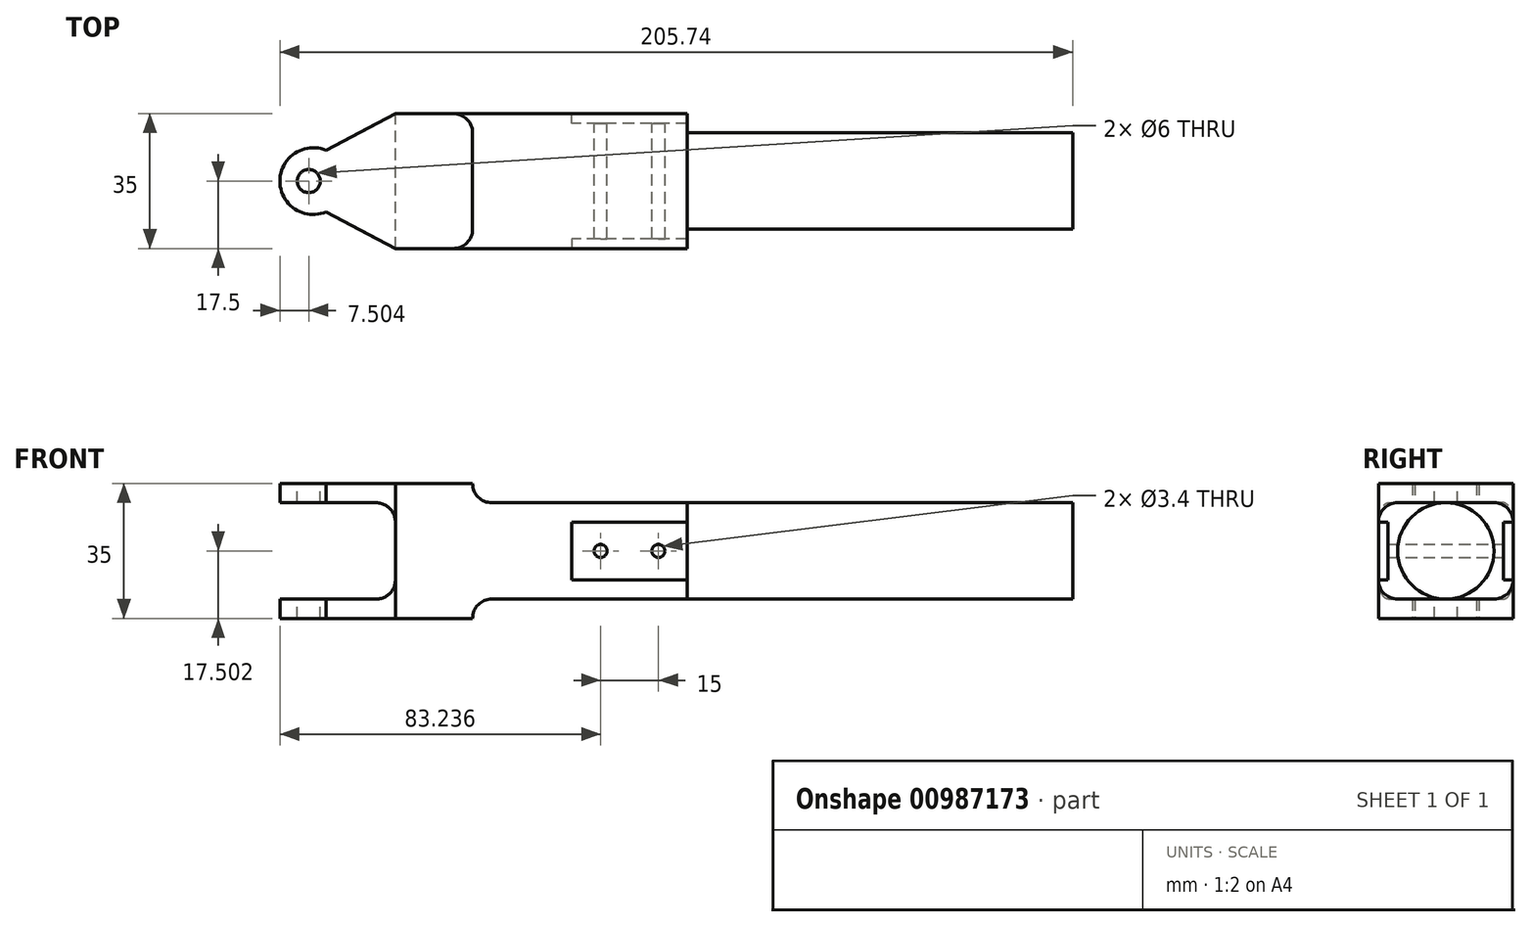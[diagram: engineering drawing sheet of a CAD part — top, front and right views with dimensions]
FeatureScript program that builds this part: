
annotation { "Feature Type Name" : "Feature", "Feature Type Description" : "" }
export const myFeature = defineFeature(function(context is Context, id is Id, definition is map)
    precondition{}
    {
        {
            var Q0;
            Q0=qCreatedBy(makeId("Front.planeOp"),FACE);
            var sketch = newSketch(context, id + "F0", { "sketchPlane" : qUnion([Q0])});
            skLineSegment(sketch, "E0.bottom", {"start": v(-12.84, 18.61) * mm, "end": v(7.16, 18.61) * mm});
            skLineSegment(sketch, "E0.top", {"start": v(-12.84, -16.39) * mm, "end": v(7.16, -16.39) * mm});
            skLineSegment(sketch, "E0.left", {"start": v(-12.84, 8.61) * mm, "end": v(-12.84, -6.39) * mm});
            skLineSegment(sketch, "E0.right", {"start": v(7.16, 18.61) * mm, "end": v(7.16, 18.61) * mm});
            skLineSegment(sketch, "E1.bottom", {"start": v(-12.84, 18.61) * mm, "end": v(-42.84, 18.61) * mm});
            skLineSegment(sketch, "E1.top", {"start": v(-17.84, 13.61) * mm, "end": v(-42.84, 13.61) * mm});
            skLineSegment(sketch, "E1.left", {"start": v(-12.84, 22.9) * mm, "end": v(-12.84, 18.61) * mm});
            skLineSegment(sketch, "E1.right", {"start": v(-42.84, 18.61) * mm, "end": v(-42.84, 13.61) * mm});
            skLineSegment(sketch, "E2.bottom", {"start": v(-12.84, -16.39) * mm, "end": v(-42.84, -16.39) * mm});
            skLineSegment(sketch, "E2.top", {"start": v(-17.84, -11.39) * mm, "end": v(-42.84, -11.39) * mm});
            skLineSegment(sketch, "E2.right", {"start": v(-42.84, -16.39) * mm, "end": v(-42.84, -11.39) * mm});
            skArc(sketch, "E3.filletArc", {"start": v(-12.84, 8.61) * mm, "mid": v(-14.3, 12.15) * mm, "end": v(-17.84, 13.61) * mm});
            skArc(sketch, "E4.filletArc", {"start": v(-17.84, -11.39) * mm, "mid": v(-14.3, -9.92) * mm, "end": v(-12.84, -6.39) * mm});
            skLineSegment(sketch, "E5.bottom", {"start": v(12.16, 13.61) * mm, "end": v(62.9, 13.61) * mm});
            skLineSegment(sketch, "E5.top", {"start": v(12.16, -11.39) * mm, "end": v(62.9, -11.39) * mm});
            skLineSegment(sketch, "E5.right", {"start": v(62.9, 13.61) * mm, "end": v(62.9, -11.39) * mm});
            skPoint(sketch, "E6.newPointB", {"position": v(7.16, -16.39) * mm});
            skArc(sketch, "E6.filletArc", {"start": v(7.16, 18.61) * mm, "mid": v(8.63, 15.08) * mm, "end": v(12.16, 13.61) * mm});
            skLineSegment(sketch, "E7", {"start": v(7.16, -16.39) * mm, "end": v(7.16, -16.39) * mm});
            skArc(sketch, "E8.filletArc", {"start": v(12.16, -11.39) * mm, "mid": v(8.63, -12.85) * mm, "end": v(7.16, -16.39) * mm});
            skSolve(sketch);
        }
        {
            var Q0;
            Q0=makeQuery(id+"F0.imprint","IMPRINT",FACE,{"disambiguationData":[TD([[makeQuery(id+"F0.imprint","IMPRINT",EDGE,{"derivedFrom":sQuery(id+"F0.wireOp",EDGE,"E0.bottom")}),-1.0]])]});
            var Q1;
            Q1 = qSketchRegion(id + "F0", true);
            extrude(context, id + "F1", {"entities" : qUnion([Q0, Q1]), "depth" : 35 * mm, "offsetDistance" : 25 * mm});
        }
        {
            var Q0;
            Q0=makeQuery(id+"F1.opExtrude","CAP_FACE",FACE,{"disambiguationData":[OSD([sQuery(id+"F0.wireOp",EDGE,"E0.bottom"),sQuery(id+"F0.wireOp",EDGE,"E0.top"),sQuery(id+"F0.wireOp",EDGE,"E0.left"),sQuery(id+"F0.wireOp",EDGE,"E1.bottom"),sQuery(id+"F0.wireOp",EDGE,"E1.top"),sQuery(id+"F0.wireOp",EDGE,"E1.right"),sQuery(id+"F0.wireOp",EDGE,"E2.bottom"),sQuery(id+"F0.wireOp",EDGE,"E2.top"),sQuery(id+"F0.wireOp",EDGE,"E2.right"),sQuery(id+"F0.wireOp",EDGE,"E3.filletArc"),sQuery(id+"F0.wireOp",EDGE,"E4.filletArc"),sQuery(id+"F0.wireOp",EDGE,"E5.bottom"),sQuery(id+"F0.wireOp",EDGE,"E5.top"),sQuery(id+"F0.wireOp",EDGE,"E5.right"),sQuery(id+"F0.wireOp",EDGE,"E6.filletArc"),sQuery(id+"F0.wireOp",EDGE,"E8.filletArc")])],"isStart":false});
            var sketch = newSketch(context, id + "F2", { "sketchPlane" : qUnion([Q0])});
            skLineSegment(sketch, "E9.bottom", {"start": v(62.9, -6.39) * mm, "end": v(32.9, -6.39) * mm});
            skLineSegment(sketch, "E9.top", {"start": v(62.9, 8.61) * mm, "end": v(32.9, 8.61) * mm});
            skLineSegment(sketch, "E9.left", {"start": v(62.9, -6.39) * mm, "end": v(62.9, 8.61) * mm});
            skLineSegment(sketch, "E9.right", {"start": v(32.9, -6.39) * mm, "end": v(32.9, 8.61) * mm});
            skSolve(sketch);
        }
        {
            var Q0;
            Q0=makeQuery(id+"F2.imprint","IMPRINT",FACE,{"disambiguationData":[TD([[makeQuery(id+"F2.imprint","IMPRINT",EDGE,{"derivedFrom":sQuery(id+"F2.wireOp",EDGE,"E9.bottom")}),-1.0]])]});
            extrude(context, id + "F3", {"entities" : qUnion([Q0]), "operationType" : NewBodyOperationType.REMOVE, "oppositeDirection" : true, "depth" : 2.5 * mm, "offsetDistance" : 25 * mm});
        }
        {
            var Q0;
            Q0=makeQuery(id+"F1.opExtrude","CAP_FACE",FACE,{"disambiguationData":[OSD([sQuery(id+"F0.wireOp",EDGE,"E0.bottom"),sQuery(id+"F0.wireOp",EDGE,"E0.top"),sQuery(id+"F0.wireOp",EDGE,"E0.left"),sQuery(id+"F0.wireOp",EDGE,"E1.bottom"),sQuery(id+"F0.wireOp",EDGE,"E1.top"),sQuery(id+"F0.wireOp",EDGE,"E1.right"),sQuery(id+"F0.wireOp",EDGE,"E2.bottom"),sQuery(id+"F0.wireOp",EDGE,"E2.top"),sQuery(id+"F0.wireOp",EDGE,"E2.right"),sQuery(id+"F0.wireOp",EDGE,"E3.filletArc"),sQuery(id+"F0.wireOp",EDGE,"E4.filletArc"),sQuery(id+"F0.wireOp",EDGE,"E5.bottom"),sQuery(id+"F0.wireOp",EDGE,"E5.top"),sQuery(id+"F0.wireOp",EDGE,"E5.right"),sQuery(id+"F0.wireOp",EDGE,"E6.filletArc"),sQuery(id+"F0.wireOp",EDGE,"E8.filletArc")])],"isStart":true});
            var sketch = newSketch(context, id + "F4", { "sketchPlane" : qUnion([Q0])});
            skLineSegment(sketch, "E10.bottom", {"start": v(-62.9, 8.61) * mm, "end": v(-32.9, 8.61) * mm});
            skLineSegment(sketch, "E10.top", {"start": v(-62.9, -6.39) * mm, "end": v(-32.9, -6.39) * mm});
            skLineSegment(sketch, "E10.left", {"start": v(-62.9, 8.61) * mm, "end": v(-62.9, -6.39) * mm});
            skLineSegment(sketch, "E10.right", {"start": v(-32.9, 8.61) * mm, "end": v(-32.9, -6.39) * mm});
            skPoint(sketch, "E11", {"position": v(-47.9, 1.11) * mm});
            skSolve(sketch);
        }
        {
            var Q0;
            Q0=makeQuery(id+"F4.imprint","IMPRINT",FACE,{"disambiguationData":[TD([[makeQuery(id+"F4.imprint","IMPRINT",EDGE,{"derivedFrom":sQuery(id+"F4.wireOp",EDGE,"E10.bottom")}),-1.0]])]});
            extrude(context, id + "F5", {"entities" : qUnion([Q0]), "operationType" : NewBodyOperationType.REMOVE, "oppositeDirection" : true, "depth" : 2.5 * mm, "offsetDistance" : 25 * mm});
        }
        {
            var Q0;
            Q0=makeQuery(id+"F5.boolean.opBoolean","COPY",FACE,{"derivedFrom":makeQuery(id+"F5.opExtrude","CAP_FACE",FACE,{"disambiguationData":[OSD([sQuery(id+"F4.wireOp",EDGE,"E10.bottom"),sQuery(id+"F4.wireOp",EDGE,"E10.top"),sQuery(id+"F4.wireOp",EDGE,"E10.left"),sQuery(id+"F4.wireOp",EDGE,"E10.right")])],"isStart":false})});
            var sketch = newSketch(context, id + "F6", { "sketchPlane" : qUnion([Q0])});
            skLineSegment(sketch, "E12", {"start": v(-32.9, 8.61) * mm, "end": v(-62.9, 8.61) * mm});
            skLineSegment(sketch, "E13", {"start": v(-62.9, 1.11) * mm, "end": v(-32.9, 1.11) * mm});
            skPoint(sketch, "E14", {"position": v(-55.4, 1.11) * mm});
            skPoint(sketch, "E15", {"position": v(-40.4, 1.11) * mm});
            skSolve(sketch);
        }
        {
            var Q0;
            Q0=sQuery(id+"F6.wireOp",VERTEX,"E14");
            var Q1;
            Q1=sQuery(id+"F6.wireOp",VERTEX,"E15");
            var Q2;
            Q2=makeQuery(id+"F1.opExtrude","SWEPT_BODY",BODY,{"disambiguationData":[OSD([sQuery(id+"F0.wireOp",EDGE,"E0.bottom"),sQuery(id+"F0.wireOp",EDGE,"E0.top"),sQuery(id+"F0.wireOp",EDGE,"E0.left"),sQuery(id+"F0.wireOp",EDGE,"E1.bottom"),sQuery(id+"F0.wireOp",EDGE,"E1.top"),sQuery(id+"F0.wireOp",EDGE,"E1.right"),sQuery(id+"F0.wireOp",EDGE,"E2.bottom"),sQuery(id+"F0.wireOp",EDGE,"E2.top"),sQuery(id+"F0.wireOp",EDGE,"E2.right"),sQuery(id+"F0.wireOp",EDGE,"E3.filletArc"),sQuery(id+"F0.wireOp",EDGE,"E4.filletArc"),sQuery(id+"F0.wireOp",EDGE,"E5.bottom"),sQuery(id+"F0.wireOp",EDGE,"E5.top"),sQuery(id+"F0.wireOp",EDGE,"E5.right"),sQuery(id+"F0.wireOp",EDGE,"E6.filletArc"),sQuery(id+"F0.wireOp",EDGE,"E8.filletArc")])]});
            hole(context, id + "F7", {"style" : HoleStyle.SIMPLE, "endStyle" : HoleEndStyle.THROUGH, "standardTappedOrClearance" : lookupTablePath({ "fit" : "Normal", "standard" : "ISO", "size" : "M3", "type" : "Clearance" }), "standardBlindInLast" : lookupTablePath({ "fit" : "Normal", "standard" : "ISO", "engagement" : "75%", "pitch" : "0.5 mm", "size" : "M3", "type" : "Clearance & tapped" }), "holeDiameter" : 3.4 * mm, "majorDiameter" : 5 * mm, "isTappedThrough" : true, "tappedDepth" : 12 * mm, "tapClearance" : 3, "locations" : qUnion([Q0, Q1]), "scope" : qUnion([Q2])});
        }
        {
            var Q0;
            Q0=makeQuery(id+"F1.opExtrude","CAP_EDGE",EDGE,{"disambiguationData":[OSD([sQuery(id+"F0.wireOp",EDGE,"E5.top")])],"isStart":true});
            var Q1;
            Q1=makeQuery(id+"F1.opExtrude","CAP_EDGE",EDGE,{"disambiguationData":[OSD([sQuery(id+"F0.wireOp",EDGE,"E5.bottom")])],"isStart":true});
            var Q2;
            Q2=makeQuery(id+"F1.opExtrude","CAP_EDGE",EDGE,{"disambiguationData":[OSD([sQuery(id+"F0.wireOp",EDGE,"E5.bottom")])],"isStart":false});
            var Q3;
            Q3=makeQuery(id+"F1.opExtrude","CAP_EDGE",EDGE,{"disambiguationData":[OSD([sQuery(id+"F0.wireOp",EDGE,"E5.top")])],"isStart":false});
            fillet(context, id + "F8", {"entities" : qUnion([Q0, Q1, Q2, Q3]), "radius" : 5 * mm, "tangentPropagation" : true, "allowEdgeOverflow" : false});
        }
        {
            var Q0;
            Q0=makeQuery(id+"F1.opExtrude","SWEPT_FACE",FACE,{"disambiguationData":[OSD([sQuery(id+"F0.wireOp",EDGE,"E0.bottom"),sQuery(id+"F0.wireOp",EDGE,"E1.bottom")])]});
            var sketch = newSketch(context, id + "F9", { "sketchPlane" : qUnion([Q0])});
            skPoint(sketch, "E16", {"position": v(-35.34, -17.5) * mm});
            skPoint(sketch, "E17", {"position": v(-12.84, -35) * mm});
            skPoint(sketch, "E18", {"position": v(-12.84, 0) * mm});
            skPoint(sketch, "E19", {"position": v(-42.84, -25) * mm});
            skPoint(sketch, "E20", {"position": v(-42.84, -10) * mm});
            skLineSegment(sketch, "E21", {"start": v(-12.84, -35) * mm, "end": v(-42.84, -25) * mm});
            skLineSegment(sketch, "E22", {"start": v(-12.84, 0) * mm, "end": v(-42.84, -10) * mm});
            skSolve(sketch);
        }
        {
            var Q0;
            Q0=sQuery(id+"F9.wireOp",VERTEX,"E16");
            var Q1;
            Q1=makeQuery(id+"F1.opExtrude","SWEPT_BODY",BODY,{"disambiguationData":[OSD([sQuery(id+"F0.wireOp",EDGE,"E0.bottom"),sQuery(id+"F0.wireOp",EDGE,"E0.top"),sQuery(id+"F0.wireOp",EDGE,"E0.left"),sQuery(id+"F0.wireOp",EDGE,"E1.bottom"),sQuery(id+"F0.wireOp",EDGE,"E1.top"),sQuery(id+"F0.wireOp",EDGE,"E1.right"),sQuery(id+"F0.wireOp",EDGE,"E2.bottom"),sQuery(id+"F0.wireOp",EDGE,"E2.top"),sQuery(id+"F0.wireOp",EDGE,"E2.right"),sQuery(id+"F0.wireOp",EDGE,"E3.filletArc"),sQuery(id+"F0.wireOp",EDGE,"E4.filletArc"),sQuery(id+"F0.wireOp",EDGE,"E5.bottom"),sQuery(id+"F0.wireOp",EDGE,"E5.top"),sQuery(id+"F0.wireOp",EDGE,"E5.right"),sQuery(id+"F0.wireOp",EDGE,"E6.filletArc"),sQuery(id+"F0.wireOp",EDGE,"E8.filletArc")])]});
            hole(context, id + "F10", {"style" : HoleStyle.SIMPLE, "endStyle" : HoleEndStyle.THROUGH, "holeDiameter" : 6 * mm, "majorDiameter" : 5 * mm, "isTappedThrough" : true, "tappedDepth" : 12 * mm, "tapClearance" : 3, "locations" : qUnion([Q0]), "scope" : qUnion([Q1])});
        }
        {
            var Q0;
            Q0=makeQuery(id+"F1.opExtrude","SWEPT_FACE",FACE,{"disambiguationData":[OSD([sQuery(id+"F0.wireOp",EDGE,"E0.top"),sQuery(id+"F0.wireOp",EDGE,"E2.bottom")])]});
            var sketch = newSketch(context, id + "F11", { "sketchPlane" : qUnion([Q0])});
            skLineSegment(sketch, "E23", {"start": v(-12.84, 0) * mm, "end": v(-12.84, 35) * mm});
            skLineSegment(sketch, "E24", {"start": v(-12.84, 0) * mm, "end": v(-30.84, 9.5) * mm});
            skLineSegment(sketch, "E25", {"start": v(-12.84, 35) * mm, "end": v(-30.84, 25.5) * mm});
            skPoint(sketch, "E26.start.orphan", {"position": v(-30.84, 0) * mm});
            skPoint(sketch, "E27.trimOffspring.end.orphan", {"position": v(-30.84, 35) * mm});
            skLineSegment(sketch, "E28", {"start": v(-30.84, 25.5) * mm, "end": v(-30.84, 9.5) * mm});
            skLineSegment(sketch, "E29", {"start": v(-42.84, 17.5) * mm, "end": v(-30.84, 17.5) * mm});
            skArc(sketch, "E30", {"start": v(-30.84, 25.5) * mm, "mid": v(-42.84, 17.5) * mm, "end": v(-30.84, 9.5) * mm});
            skSolve(sketch);
        }
        {
            var Q0;
            {var subQ0=sQuery(id+"F11.wireOp",EDGE,"E24");Q0=makeQuery(id+"F11.imprint","IMPRINT",FACE,{"disambiguationData":[TD([[makeQuery(id+"F11.imprint","IMPRINT",EDGE,{"derivedFrom":subQ0}),1.0]])]});}
            var Q1;
            {var subQ0=sQuery(id+"F11.wireOp",EDGE,"E25");Q1=makeQuery(id+"F11.imprint","IMPRINT",FACE,{"disambiguationData":[TD([[makeQuery(id+"F11.imprint","IMPRINT",EDGE,{"derivedFrom":subQ0}),-1.0]])]});}
            extrude(context, id + "F12", {"entities" : qUnion([Q0, Q1]), "operationType" : NewBodyOperationType.REMOVE, "oppositeDirection" : true, "depth" : 35 * mm, "offsetDistance" : 25 * mm});
        }
        {
            var Q0;
            Q0=makeQuery(id+"F1.opExtrude","SWEPT_FACE",FACE,{"disambiguationData":[OSD([sQuery(id+"F0.wireOp",EDGE,"E5.right")])]});
            var sketch = newSketch(context, id + "F13", { "sketchPlane" : qUnion([Q0])});
            skCircle(sketch, "E31", {"center": v(-17.5, 1.11) * mm, "radius": 12.5 * mm});
            skPoint(sketch, "E32.orphan", {"position": v(-2.5, 1.11) * mm});
            skPoint(sketch, "E33.orphan", {"position": v(-32.5, 1.11) * mm});
            skSolve(sketch);
        }
        {
            var Q0;
            {var subQ0=sQuery(id+"F13.wireOp",EDGE,"E31");var subQ1=sQuery(id+"F0.wireOp",EDGE,"E5.right");var subQ2=makeQuery(id+"F13.imprint","INTERSECT",VERTEX,{"derivedFrom":[makeQuery(id+"F1.opExtrude","SWEPT_EDGE",EDGE,{"disambiguationData":[OSD([sQuery(id+"F0.wireOp",EDGE,"E5.bottom"),subQ1])]}),subQ0]});Q0=makeQuery(id+"F13.imprint","IMPRINT",FACE,{"disambiguationData":[TD([[makeQuery(id+"F13.imprint","IMPRINT",EDGE,{"disambiguationData":[TD([[subQ2,-1.0]])],"derivedFrom":subQ0}),1.0]])]});}
            extrude(context, id + "F14", {"entities" : qUnion([Q0]), "operationType" : NewBodyOperationType.ADD, "depth" : 100 * mm, "offsetDistance" : 25 * mm});
        }
    });
